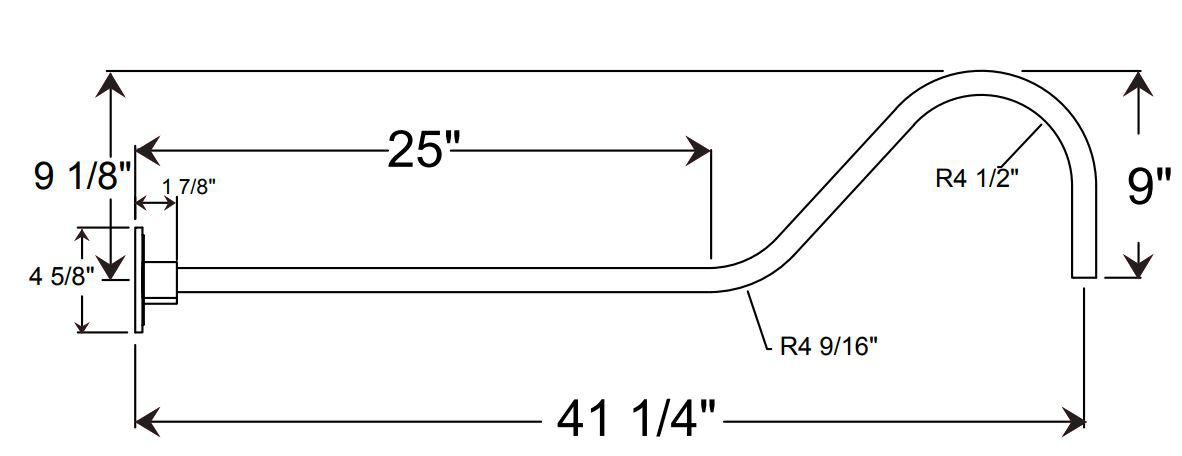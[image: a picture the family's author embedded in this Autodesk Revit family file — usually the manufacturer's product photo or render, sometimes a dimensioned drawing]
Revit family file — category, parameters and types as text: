
# Revit family: BISTRO(8,12,14,16,18) LED
name_source: partatom
category: Lighting Fixtures
units: mm (PartAtom-declared; Revit-internal decimal feet)

## family parameters
Always vertical = Yes
Cut with Voids When Loaded = No
Light Source = Yes
OmniClass Number = 23.80.70.00
OmniClass Title = Lighting
Part Type = Normal
Room Calculation Point = No
Round Connector Dimension = Use Diameter
Shared = No
Work Plane-Based = No

## types (5) — shared parameters
Body Colour = Spun aluminium
Body Material = body
CRI = >90
Color Filter = 16777215
Construction Material = Heavy Duty spun aluminum.
Default Elevation = 0' - 0"
Description = 120-277 Voltage
Dimming = 1%
Dimming Lamp Color Temperature Shift = <None>
Efficiency = 65-125 lumens per watt
Lamp = LED
Life = L70 50,000 hours
Load Classification = Lighting
Manufacturer = ANP Lighting
Photometric Web File = BB14-100GLCL-32WPL.ies
Power Factor = 1
Tilt Angle = 90.00°
URL = https://www.anplighting.com
Voltage = 277 V
Warranty = 5 year limited warranty

## per-type parameters (varying)
| type | Apparent Load | BB08 | BB12 | BB14 | BB16 | BB18 | Fixture Diameter | Fixture Height | Model | Wattage Comments | Weight |
| BB08 | 9 VA | Yes | No | No | No | No | 0' - 8" | 0' - 6" | BB 08 | 9W | 1 lbs |
| BB12 | 16 VA | No | Yes | No | No | No | 1' - 0" | 0' - 8 1/2" | BB 12 | 16W | 1.5 lbs |
| BB14 | 16 VA | No | No | Yes | No | No | 1' - 2" | 0' - 10" | BB 14 | 16W | 1.5 lbs |
| BB16 | 16 VA | No | No | No | Yes | No | 1' - 4" | 0' - 10" | BB 16 | 16W | 1.5 lbs |
| BB18 | 16 VA | No | No | No | No | Yes | 1' - 6" | 0' - 11" | BB 18 | 16W | 2.5 lbs |

## geometry (parser evidence)
native form markers: Sweep x32
no freeform markers — native parametric forms only
